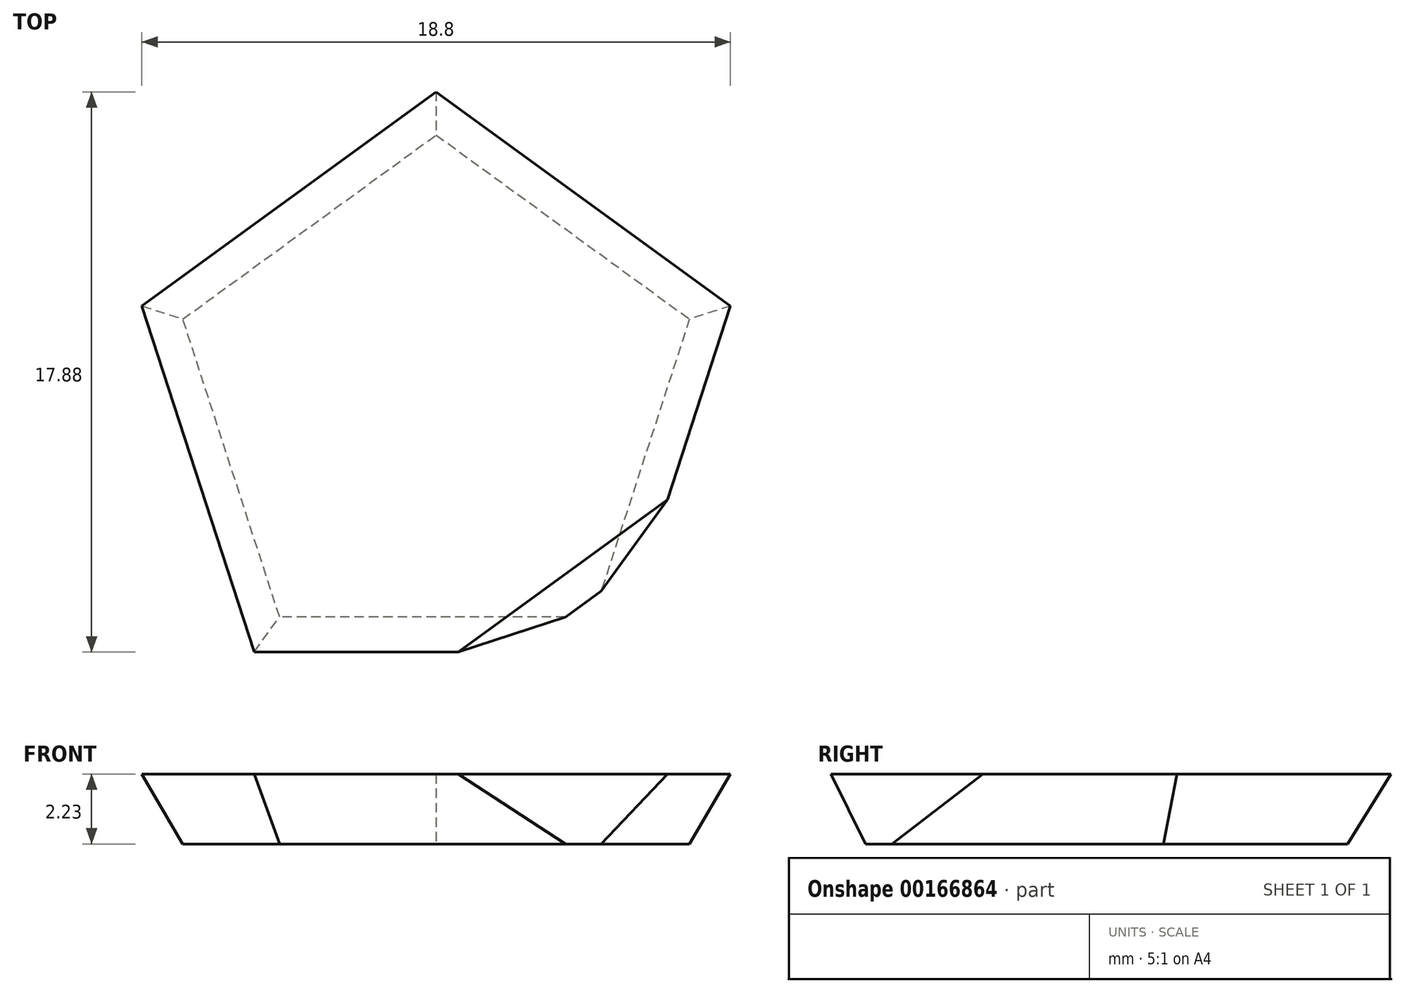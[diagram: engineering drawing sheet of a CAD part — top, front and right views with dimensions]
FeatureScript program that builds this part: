
annotation { "Feature Type Name" : "Feature", "Feature Type Description" : "" }
export const myFeature = defineFeature(function(context is Context, id is Id, definition is map)
    precondition{}
    {
        {
            var Q0;
            Q0=qCreatedBy(makeId("Top.planeOp"),FACE);
            var sketch = newSketch(context, id + "F0", { "sketchPlane" : qUnion([Q0])});
            skCircle(sketch, "E0.cCircle", {"center": v(0, 0) * mm, "radius": 6.88 * mm, "construction": true});
            skLineSegment(sketch, "E0.0", {"start": v(-8.1, 2.63) * mm, "end": v(0, 8.5) * mm});
            skLineSegment(sketch, "E0.1", {"start": v(0, 8.5) * mm, "end": v(8.1, 2.63) * mm});
            skLineSegment(sketch, "E0.2", {"start": v(8.1, 2.63) * mm, "end": v(5, -6.88) * mm});
            skLineSegment(sketch, "E0.3", {"start": v(5, -6.88) * mm, "end": v(-5, -6.88) * mm});
            skLineSegment(sketch, "E0.4", {"start": v(-5, -6.88) * mm, "end": v(-8.1, 2.63) * mm});
            skPoint(sketch, "E0.0.midPoint", {"position": v(-4.05, 5.57) * mm});
            skSolve(sketch);
        }
        {
            var Q0;
            Q0 = qSketchRegion(id + "F0", true);
            extrude(context, id + "F1", {"entities" : qUnion([Q0]), "depth" : ((1 / sin(36 * degree)) * (sin(18 * degree) + 1)) * mm, "hasDraft" : true, "draftAngle" : acos(-1 / sqrt(5)) - 90 * degree});
        }
        {
            var Q0;
            Q0=makeQuery(id+"F1.opExtrude","CAP_FACE",FACE,{"disambiguationData":[OSD([sQuery(id+"F0.wireOp",EDGE,"E0.0"),sQuery(id+"F0.wireOp",EDGE,"E0.1"),sQuery(id+"F0.wireOp",EDGE,"E0.2"),sQuery(id+"F0.wireOp",EDGE,"E0.3"),sQuery(id+"F0.wireOp",EDGE,"E0.4")])],"isStart":false});
            var sketch = newSketch(context, id + "F2", { "sketchPlane" : qUnion([Q0])});
            skCircle(sketch, "E1.cCircle", {"center": v(0, 0) * mm, "radius": 6.88 * mm, "construction": true});
            skLineSegment(sketch, "E1.0", {"start": v(8.1, -2.63) * mm, "end": v(0, -8.5) * mm});
            skLineSegment(sketch, "E1.1", {"start": v(0, -8.5) * mm, "end": v(-8.1, -2.63) * mm});
            skLineSegment(sketch, "E1.2", {"start": v(-8.1, -2.63) * mm, "end": v(-5, 6.88) * mm});
            skLineSegment(sketch, "E1.3", {"start": v(-5, 6.88) * mm, "end": v(5, 6.88) * mm});
            skLineSegment(sketch, "E1.4", {"start": v(5, 6.88) * mm, "end": v(8.1, -2.63) * mm});
            skPoint(sketch, "E1.0.midPoint", {"position": v(4.05, -5.57) * mm});
            skSolve(sketch);
        }
        {
            var Q0;
            Q0=makeQuery(id+"F2.imprint","IMPRINT",FACE,{"disambiguationData":[TD([[makeQuery(id+"F2.imprint","IMPRINT",EDGE,{"derivedFrom":sQuery(id+"F2.wireOp",EDGE,"E1.0")}),1.0]])]});
            extrude(context, id + "F3", {"entities" : qUnion([Q0]), "operationType" : NewBodyOperationType.REMOVE, "endBound" : BoundingType.THROUGH_ALL, "oppositeDirection" : true, "depth" : ((1 / sin(36 * degree)) * (sin(18 * degree) + 1)) * mm, "hasDraft" : true, "draftAngle" : acos(-1 / sqrt(5)) - 90 * degree, "draftPullDirection" : true});
        }
    });
